# Revit family: Sanitary_Hand-Hair-Dryers_JVD_NEPTUNE_
name_source: partatom
category: Specialty Equipment
units: mm (PartAtom-declared; Revit-internal decimal feet)

## family parameters
Cut with Voids When Loaded = No
Host = Face
OmniClass Number = 23.31.25.15
OmniClass Title = Hand Dryers
Part Type = Normal
Room Calculation Point = No
Round Connector Dimension = Use Diameter
Shared = No

## types (4) — shared parameters
Air outlet temperature (°C) = 50
Apparent Load = 2000 VA
Connector Description = Electrical Connection
Current = 1 A
Depth = 411 mm
Description = NEPTUNE hair dryer for pools and gyms, resistant in chlorinated atmosphere and provided with an induction motor for intensive use. Adjustable and ergonomic height (180 ° rotation).
Diffusor = No
Frequency (Hz) = 50
Height = 1153 mm
Manufacturer = JVD
Material = ABS & Polycarbonate
Model = NEPTUNE
Number of Poles = 1
ON/OFF switch = Yes
Power Factor = 1
Product data url = https://bimobject.com
Safety in case of malfunction = Yes
Shaver socket = Without
Speed control = 1 speed
Temperature variation = 1
Type of motor = Induction
URL = www.jvd.fr/en/
Vandal-safe = Yes
Voltage = 230 V
Weight = 3.07 kg
Width = 150 mm
zero-valued in all types: Default Elevation, Edition number, Version

## per-type parameters (varying)
| type | Colour |
| 8221405 NEPTUNE White | JVD - Plastic - White - RAL 9016 |
| 8221762 NEPTUNE Matte Black | JVD - Plastic - Matte Black - RAL 9005 |
| 8221406 NEPTUNE Blue | JVD - Plastic - Blue |
| 8221407 NEPTUNE Red | JVD - Plastic - Red - RAL 3001 |

## geometry (parser evidence)
native form markers: Sweep x3
no freeform markers — native parametric forms only
